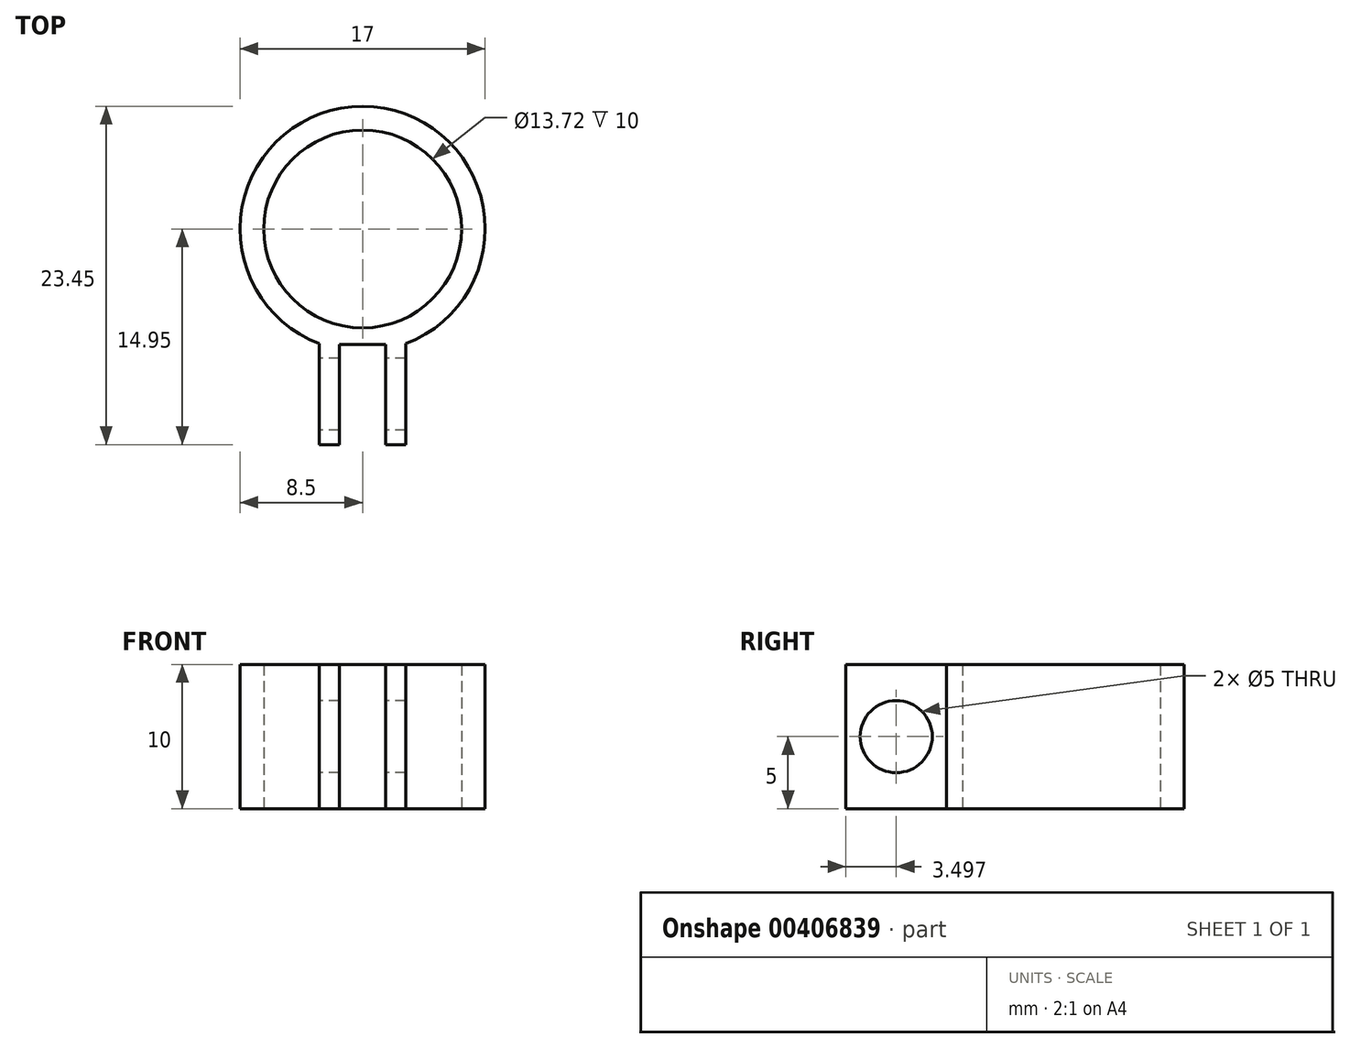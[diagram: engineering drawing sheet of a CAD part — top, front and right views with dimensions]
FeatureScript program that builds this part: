
annotation { "Feature Type Name" : "Feature", "Feature Type Description" : "" }
export const myFeature = defineFeature(function(context is Context, id is Id, definition is map)
    precondition{}
    {
        {
            var Q0;
            Q0=qCreatedBy(makeId("Top.planeOp"),FACE);
            var sketch = newSketch(context, id + "F0", { "sketchPlane" : qUnion([Q0])});
            skArc(sketch, "E0", {"start": v(3, -7.95) * mm, "mid": v(0, 8.5) * mm, "end": v(-3, -7.95) * mm});
            skCircle(sketch, "E1", {"center": v(0, 0) * mm, "radius": 6.86 * mm});
            skLineSegment(sketch, "E2.left", {"start": v(-3, -7.95) * mm, "end": v(-3, -14.95) * mm});
            skLineSegment(sketch, "E2.right", {"start": v(3, -7.95) * mm, "end": v(3, -14.95) * mm});
            skLineSegment(sketch, "E3.top", {"start": v(-1.6, -8) * mm, "end": v(1.6, -8) * mm});
            skLineSegment(sketch, "E3.left", {"start": v(-1.6, -14.95) * mm, "end": v(-1.6, -8) * mm});
            skLineSegment(sketch, "E3.right", {"start": v(1.6, -14.95) * mm, "end": v(1.6, -8) * mm});
            skLineSegment(sketch, "E4", {"start": v(-3, -14.95) * mm, "end": v(-1.6, -14.95) * mm});
            skLineSegment(sketch, "E5", {"start": v(1.6, -14.95) * mm, "end": v(3, -14.95) * mm});
            skSolve(sketch);
        }
        {
            var Q0;
            Q0 = qSketchRegion(id + "F0", true);
            extrude(context, id + "F1", {"entities" : qUnion([Q0]), "depth" : 10 * mm});
        }
        {
            var Q0;
            Q0=makeQuery(id+"F1.opExtrude","SWEPT_FACE",FACE,{"disambiguationData":[OSD([sQuery(id+"F0.wireOp",EDGE,"E2.left")])]});
            var sketch = newSketch(context, id + "F2", { "sketchPlane" : qUnion([Q0])});
            skLineSegment(sketch, "E6", {"start": v(14.95, 10) * mm, "end": v(7.95, 0) * mm, "construction": true});
            skLineSegment(sketch, "E7", {"start": v(7.95, 10) * mm, "end": v(14.95, 0) * mm, "construction": true});
            skCircle(sketch, "E8", {"center": v(11.45, 5) * mm, "radius": 2.5 * mm});
            skSolve(sketch);
        }
        {
            var Q0;
            Q0 = qSketchRegion(id + "F2", true);
            extrude(context, id + "F3", {"entities" : qUnion([Q0]), "operationType" : NewBodyOperationType.REMOVE, "endBound" : BoundingType.THROUGH_ALL, "oppositeDirection" : true, "depth" : 25 * mm});
        }
    });
